# Revit family: RN 86003-xx Optiflex-Verteiler gerade
name_source: partatom
category: HLS-Bauteile
units: mm (PartAtom-declared; Revit-internal decimal feet)

## family parameters
Arbeitsebenenbasiert = Nein
Beim Laden mit Abzugskörper schneiden = Nein
Bemaßung runder Anschluss = Durchmesser verwenden
Gemeinsam genutzt = Nein
Immer vertikal = Ja
Klassifizierung = Keine
Raumberechnungspunkt = Nein
Teiletyp = Normal

## types (8) — shared parameters
G1 = 20 mm  [stored 0.0656168 ft]
Hersteller = R. Nussbaum AG
L2 = 58 mm  [stored 0.190289 ft]
L3 = 28 mm  [stored 0.0918635 ft]
RN_tab = RN_86003
Verbindung_1_Durchmesser = 25 mm  [stored 0.082021 ft]
Verbindung_2_Durchmesser = 20 mm  [stored 0.0656168 ft]
Verbindung_3_Durchmesser = 20 mm  [stored 0.0656168 ft]
Verbindung_4_Durchmesser = 25 mm  [stored 0.082021 ft]
zero-valued in all types: vpindex

## per-type parameters (varying)
| type | Beschreibung | DN1 | L4 | L5 | N | RN_Beschreibung | Typenkommentare | URL | p1 | p2 | p3 | p4 | p5 | p6 | p7 | p8 | pindex | z | z1 |
| 86003.22 | DN20x2 | 20 mm  [stored 0.0656168 ft] | 128 mm | 32 mm | 2 | DN20x2 | 86003.22 Optiflex-Verteiler gerade, 2 - fach mit Innengewinde und Aussengewinde |  | Ja | Nein | Nein | Nein | Nein | Nein | Nein | Nein | 1 | 13 mm | 15 mm  [stored 0.0492126 ft] |
| 86003.23 | DN20x3 | 20 mm  [stored 0.0656168 ft] | 186 mm | 32 mm | 3 | DN20x3 | 86003.23 Optiflex-Verteiler gerade, 3 - fach mit Innengewinde und Aussengewinde |  | Nein | Ja | Nein | Nein | Nein | Nein | Nein | Nein | 2 | 13 mm | 15 mm  [stored 0.0492126 ft] |
| 86003.24 | DN20x4 | 20 mm  [stored 0.0656168 ft] | 244 mm  [stored 0.800525 ft] | 32 mm | 4 | DN20x4 | 86003.24 Optiflex-Verteiler gerade, 4 - fach mit Innengewinde und Aussengewinde |  | Nein | Nein | Ja | Nein | Nein | Nein | Nein | Nein | 3 | 13 mm | 15 mm  [stored 0.0492126 ft] |
| 86003.25 | DN20x5 | 20 mm  [stored 0.0656168 ft] | 302 mm  [stored 0.990814 ft] | 32 mm | 5 | DN20x5 | 86003.25 Optiflex-Verteiler gerade, 5 - fach mit Innengewinde und Aussengewinde |  | Nein | Nein | Nein | Ja | Nein | Nein | Nein | Nein | 4 | 13 mm | 15 mm  [stored 0.0492126 ft] |
| 86003.32 | DN25x2 | 25 mm  [stored 0.082021 ft] | 132 mm | 36 mm  [stored 0.11811 ft] | 2 | DN25x2 | 86003.32 Optiflex-Verteiler gerade, 2 - fach mit Innengewinde und Aussengewinde |  | Nein | Nein | Nein | Nein | Ja | Nein | Nein | Nein | 5 | 10 mm  [stored 0.0328084 ft] | 20 mm  [stored 0.0656168 ft] |
| 86003.33 | DN25x3 | 25 mm  [stored 0.082021 ft] | 190 mm | 36 mm  [stored 0.11811 ft] | 3 | DN25x3 | 86003.33 Optiflex-Verteiler gerade, 3 - fach mit Innengewinde und Aussengewinde |  | Nein | Nein | Nein | Nein | Nein | Ja | Nein | Nein | 6 | 10 mm  [stored 0.0328084 ft] | 20 mm  [stored 0.0656168 ft] |
| 86003.34 | DN25x4 | 25 mm  [stored 0.082021 ft] | 248 mm | 36 mm  [stored 0.11811 ft] | 4 | DN25x4 | 86003.34 Optiflex-Verteiler gerade, 4 - fach mit Innengewinde und Aussengewinde |  | Nein | Nein | Nein | Nein | Nein | Nein | Ja | Nein | 7 | 10 mm  [stored 0.0328084 ft] | 20 mm  [stored 0.0656168 ft] |
| 86003.35 | DN25x5 | 25 mm  [stored 0.082021 ft] | 306 mm | 36 mm  [stored 0.11811 ft] | 5 | DN25x5 | 86003.35 Optiflex-Verteiler gerade, 5 - fach mit Innengewinde und Aussengewinde | https://www.nussbaum.ch | Nein | Nein | Nein | Nein | Nein | Nein | Nein | Ja | 8 | 10 mm  [stored 0.0328084 ft] | 20 mm  [stored 0.0656168 ft] |

note: column(s) folded — value = type name in every type: RN_ArtNr

note: [stored X ft] marks values corroborated as IEEE doubles in the binary element streams (Revit-internal decimal feet)
